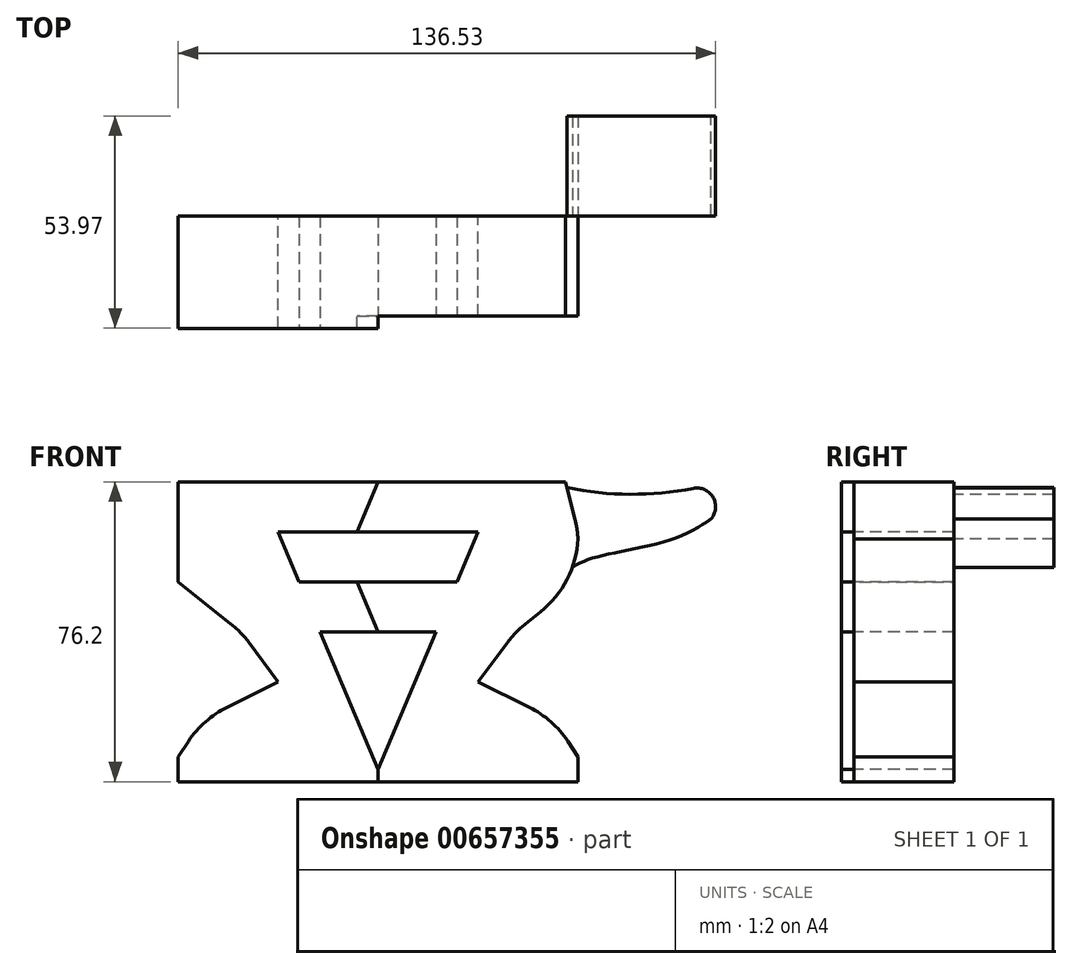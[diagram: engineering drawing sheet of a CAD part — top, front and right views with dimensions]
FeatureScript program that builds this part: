
annotation { "Feature Type Name" : "Feature", "Feature Type Description" : "" }
export const myFeature = defineFeature(function(context is Context, id is Id, definition is map)
    precondition{}
    {
        {
            var Q0;
            Q0=qCreatedBy(makeId("Front.planeOp"),FACE);
            var sketch = newSketch(context, id + "F0", { "sketchPlane" : qUnion([Q0])});
            skLineSegment(sketch, "E0.bottom", {"start": v(50.8, 38.1) * mm, "end": v(-50.8, 38.1) * mm, "construction": true});
            skLineSegment(sketch, "E0.top", {"start": v(50.8, -38.1) * mm, "end": v(-50.8, -38.1) * mm});
            skLineSegment(sketch, "E0.left", {"start": v(50.8, 38.1) * mm, "end": v(50.8, -38.1) * mm, "construction": true});
            skLineSegment(sketch, "E0.right", {"start": v(-50.8, 38.1) * mm, "end": v(-50.8, -38.1) * mm, "construction": true});
            skPoint(sketch, "E0.middle", {"position": v(0, 0) * mm});
            skLineSegment(sketch, "E1", {"start": v(0, 38.1) * mm, "end": v(0, -38.1) * mm, "construction": true});
            skLineSegment(sketch, "E2", {"start": v(-50.8, 0) * mm, "end": v(50.8, 0) * mm, "construction": true});
            skLineSegment(sketch, "E3", {"start": v(-50.8, 12.7) * mm, "end": v(50.8, 12.7) * mm, "construction": true});
            skLineSegment(sketch, "E4", {"start": v(-50.8, -12.7) * mm, "end": v(50.8, -12.7) * mm, "construction": true});
            skLineSegment(sketch, "E5", {"start": v(-25.4, 38.1) * mm, "end": v(-25.4, -38.1) * mm, "construction": true});
            skLineSegment(sketch, "E6", {"start": v(25.4, 38.1) * mm, "end": v(25.4, -38.1) * mm, "construction": true});
            skLineSegment(sketch, "E7", {"start": v(-50.8, 38.1) * mm, "end": v(-50.8, 12.7) * mm});
            skLineSegment(sketch, "E8", {"start": v(50.8, 38.1) * mm, "end": v(50.8, 12.7) * mm});
            skLineSegment(sketch, "E9", {"start": v(-50.8, 38.1) * mm, "end": v(50.8, 38.1) * mm});
            skLineSegment(sketch, "E10", {"start": v(-50.8, 12.7) * mm, "end": v(-25.4, -12.7) * mm, "construction": true});
            skLineSegment(sketch, "E11", {"start": v(50.8, 12.7) * mm, "end": v(25.4, -12.7) * mm, "construction": true});
            skLineSegment(sketch, "E12", {"start": v(-25.4, -12.7) * mm, "end": v(-50.8, -31.75) * mm, "construction": true});
            skLineSegment(sketch, "E13", {"start": v(-50.8, -31.75) * mm, "end": v(-50.8, -38.1) * mm});
            skLineSegment(sketch, "E14", {"start": v(25.4, -12.7) * mm, "end": v(50.8, -31.75) * mm, "construction": true});
            skLineSegment(sketch, "E15", {"start": v(50.8, -31.75) * mm, "end": v(50.8, -38.1) * mm});
            skLineSegment(sketch, "E16", {"start": v(-50.8, -38.1) * mm, "end": v(50.8, -38.1) * mm});
            skLineSegment(sketch, "E17", {"start": v(-50.8, 25.4) * mm, "end": v(50.8, 25.4) * mm, "construction": true});
            skLineSegment(sketch, "E18", {"start": v(-50.8, -31.75) * mm, "end": v(50.8, -31.75) * mm, "construction": true});
            skLineSegment(sketch, "E19", {"start": v(47.63, 38.1) * mm, "end": v(50.8, 25.4) * mm});
            skLineSegment(sketch, "E20", {"start": v(50.8, 12.7) * mm, "end": v(34.93, 0) * mm});
            skLineSegment(sketch, "E21", {"start": v(34.93, 0) * mm, "end": v(25.4, -12.7) * mm});
            skLineSegment(sketch, "E22", {"start": v(-50.8, 12.7) * mm, "end": v(-34.93, 0) * mm});
            skLineSegment(sketch, "E23", {"start": v(-34.93, 0) * mm, "end": v(-25.4, -12.7) * mm});
            skLineSegment(sketch, "E24", {"start": v(25.4, -12.7) * mm, "end": v(44.45, -22.22) * mm});
            skLineSegment(sketch, "E25", {"start": v(44.45, -22.22) * mm, "end": v(50.8, -31.75) * mm});
            skLineSegment(sketch, "E26", {"start": v(-25.4, -12.7) * mm, "end": v(-44.45, -22.22) * mm});
            skLineSegment(sketch, "E27", {"start": v(-44.45, -22.22) * mm, "end": v(-50.8, -31.75) * mm});
            skLineSegment(sketch, "E28", {"start": v(-50.8, -22.23) * mm, "end": v(50.8, -22.22) * mm, "construction": true});
            skSolve(sketch);
        }
        {
            var Q0;
            {var subQ2=sQuery(id+"F0.wireOp",EDGE,"E7");Q0=makeQuery(id+"F0.imprint","IMPRINT",FACE,{"disambiguationData":[TD([[makeQuery(id+"F0.imprint","IMPRINT",EDGE,{"derivedFrom":subQ2}),1.0]])]});}
            extrude(context, id + "F1", {"entities" : qUnion([Q0]), "depth" : 25.4 * mm, "offsetDistance" : 25.4 * mm});
        }
        {
            var Q0;
            Q0=makeQuery(id+"F1.opExtrude","SWEPT_EDGE",EDGE,{"disambiguationData":[OSD([sQuery(id+"F0.wireOp",EDGE,"E8"),sQuery(id+"F0.wireOp",EDGE,"E19")])]});
            var Q1;
            Q1=makeQuery(id+"F1.opExtrude","SWEPT_EDGE",EDGE,{"disambiguationData":[OSD([sQuery(id+"F0.wireOp",EDGE,"E8"),sQuery(id+"F0.wireOp",EDGE,"E20")])]});
            var Q2;
            Q2=makeQuery(id+"F1.opExtrude","SWEPT_EDGE",EDGE,{"disambiguationData":[OSD([sQuery(id+"F0.wireOp",EDGE,"E24"),sQuery(id+"F0.wireOp",EDGE,"E25")])]});
            var Q3;
            Q3=makeQuery(id+"F1.opExtrude","SWEPT_EDGE",EDGE,{"disambiguationData":[OSD([sQuery(id+"F0.wireOp",EDGE,"E20"),sQuery(id+"F0.wireOp",EDGE,"E21")])]});
            fillet(context, id + "F2", {"entities" : qUnion([Q0, Q1, Q2, Q3]), "radius" : 25.4 * mm, "tangentPropagation" : true, "allowEdgeOverflow" : false});
        }
        {
            var Q0;
            Q0=makeQuery(id+"F1.opExtrude","CAP_FACE",FACE,{"disambiguationData":[OSD([sQuery(id+"F0.wireOp",EDGE,"E7"),sQuery(id+"F0.wireOp",EDGE,"E8"),sQuery(id+"F0.wireOp",EDGE,"E9"),sQuery(id+"F0.wireOp",EDGE,"E13"),sQuery(id+"F0.wireOp",EDGE,"E15"),sQuery(id+"F0.wireOp",EDGE,"E16"),sQuery(id+"F0.wireOp",EDGE,"E19"),sQuery(id+"F0.wireOp",EDGE,"E20"),sQuery(id+"F0.wireOp",EDGE,"E21"),sQuery(id+"F0.wireOp",EDGE,"E22"),sQuery(id+"F0.wireOp",EDGE,"E23"),sQuery(id+"F0.wireOp",EDGE,"E24"),sQuery(id+"F0.wireOp",EDGE,"E25"),sQuery(id+"F0.wireOp",EDGE,"E26"),sQuery(id+"F0.wireOp",EDGE,"E27")])],"isStart":true});
            var sketch = newSketch(context, id + "F3", { "sketchPlane" : qUnion([Q0])});
            skLineSegment(sketch, "E29.bottom", {"start": v(-47.63, 38.1) * mm, "end": v(-85.72, 38.1) * mm, "construction": true});
            skLineSegment(sketch, "E29.top", {"start": v(-47.62, 12.7) * mm, "end": v(-85.72, 12.7) * mm, "construction": true});
            skLineSegment(sketch, "E29.left", {"start": v(-47.63, 38.1) * mm, "end": v(-47.63, 12.7) * mm, "construction": true});
            skLineSegment(sketch, "E29.right", {"start": v(-85.72, 38.1) * mm, "end": v(-85.72, 12.7) * mm, "construction": true});
            skLineSegment(sketch, "E30", {"start": v(-47.62, 34.92) * mm, "end": v(-85.72, 34.92) * mm, "construction": true});
            skArc(sketch, "E31", {"start": v(-80.05, 36.43) * mm, "mid": v(-85.61, 32.79) * mm, "end": v(-82.13, 27.13) * mm});
            skArc(sketch, "E32", {"start": v(-80.5, 36.51) * mm, "mid": v(-64.05, 34.93) * mm, "end": v(-47.63, 36.68) * mm});
            skLineSegment(sketch, "E33", {"start": v(-48.42, 34.92) * mm, "end": v(-48.42, 38.1) * mm, "construction": true});
            skPoint(sketch, "E34", {"position": v(-48.42, 36.51) * mm});
            skLineSegment(sketch, "E35", {"start": v(-48.42, 36.51) * mm, "end": v(-85.72, 36.51) * mm, "construction": true});
            skCircle(sketch, "E36", {"center": v(-113.4, -96.09) * mm, "radius": 127.13 * mm, "construction": true});
            skCircle(sketch, "E37", {"center": v(-80.96, 31.75) * mm, "radius": 4.76 * mm, "construction": true});
            skFitSpline(sketch, "E38", {"points": [v(-49.32, 16.36) * mm, v(-56.41, 19.23) * mm, v(-72.92, 22.96) * mm, v(-84.58, 28.66) * mm], "startDerivative": vector(-24.27, 15.2) * mm, "endDerivative": vector(-28.85, 20.7) * mm});
            skSolve(sketch);
        }
        {
            var Q0;
            {var subQ1=sQuery(id+"F3.wireOp",EDGE,"E31");var subQ10=sQuery(id+"F3.wireOp",EDGE,"E32");var subQ14=makeQuery(id+"F3.imprint","INTERSECT",VERTEX,{"derivedFrom":[subQ1,subQ10]});Q0=makeQuery(id+"F3.imprint","IMPRINT",FACE,{"disambiguationData":[TD([[makeQuery(id+"F3.imprint","IMPRINT",EDGE,{"disambiguationData":[TD([[subQ14,-1.0]])],"derivedFrom":subQ1}),1.0]])]});}
            extrude(context, id + "F4", {"entities" : qUnion([Q0]), "depth" : 25.4 * mm, "offsetDistance" : 25.4 * mm});
        }
        {
            var Q0;
            Q0=makeQuery(id+"F1.opExtrude","CAP_FACE",FACE,{"disambiguationData":[OSD([sQuery(id+"F0.wireOp",EDGE,"E7"),sQuery(id+"F0.wireOp",EDGE,"E8"),sQuery(id+"F0.wireOp",EDGE,"E9"),sQuery(id+"F0.wireOp",EDGE,"E13"),sQuery(id+"F0.wireOp",EDGE,"E15"),sQuery(id+"F0.wireOp",EDGE,"E16"),sQuery(id+"F0.wireOp",EDGE,"E19"),sQuery(id+"F0.wireOp",EDGE,"E20"),sQuery(id+"F0.wireOp",EDGE,"E21"),sQuery(id+"F0.wireOp",EDGE,"E22"),sQuery(id+"F0.wireOp",EDGE,"E23"),sQuery(id+"F0.wireOp",EDGE,"E24"),sQuery(id+"F0.wireOp",EDGE,"E25"),sQuery(id+"F0.wireOp",EDGE,"E26"),sQuery(id+"F0.wireOp",EDGE,"E27")])],"isStart":false});
            var sketch = newSketch(context, id + "F5", { "sketchPlane" : qUnion([Q0])});
            skLineSegment(sketch, "E39", {"start": v(0, 38.1) * mm, "end": v(0, -38.1) * mm, "construction": true});
            skLineSegment(sketch, "E40", {"start": v(-35.2, 0) * mm, "end": v(35.2, 0) * mm, "construction": true});
            skLineSegment(sketch, "E41", {"start": v(-50.8, 25.4) * mm, "end": v(50.04, 25.4) * mm, "construction": true});
            skLineSegment(sketch, "E42", {"start": v(-50.8, 12.7) * mm, "end": v(47.67, 12.7) * mm, "construction": true});
            skLineSegment(sketch, "E43", {"start": v(-25.4, 25.4) * mm, "end": v(25.4, 25.4) * mm});
            skLineSegment(sketch, "E44", {"start": v(20.05, 12.7) * mm, "end": v(-20.05, 12.7) * mm});
            skLineSegment(sketch, "E45", {"start": v(-14.7, 0) * mm, "end": v(14.7, 0) * mm});
            skLineSegment(sketch, "E46", {"start": v(25.4, 25.4) * mm, "end": v(0, -34.93) * mm, "construction": true});
            skLineSegment(sketch, "E47", {"start": v(0, -34.93) * mm, "end": v(-25.4, 25.4) * mm, "construction": true});
            skLineSegment(sketch, "E48", {"start": v(-10.07, -11) * mm, "end": v(10.07, -11) * mm, "construction": true});
            skPoint(sketch, "E49", {"position": v(0, -11) * mm});
            skLineSegment(sketch, "E50", {"start": v(-25.4, 25.4) * mm, "end": v(-20.05, 12.7) * mm});
            skLineSegment(sketch, "E51", {"start": v(25.4, 25.4) * mm, "end": v(20.05, 12.7) * mm});
            skLineSegment(sketch, "E52", {"start": v(-14.7, 0) * mm, "end": v(0, -34.93) * mm});
            skLineSegment(sketch, "E53", {"start": v(14.7, 0) * mm, "end": v(0, -34.93) * mm});
            skSolve(sketch);
        }
        {
            var Q0;
            Q0 = qSketchRegion(id + "F5", true);
            extrude(context, id + "F6", {"entities" : qUnion([Q0]), "operationType" : NewBodyOperationType.REMOVE, "endBound" : BoundingType.THROUGH_ALL, "oppositeDirection" : true, "depth" : 6.35 * mm, "offsetDistance" : 25.4 * mm});
        }
        {
            var Q0;
            Q0=makeQuery(id+"F1.opExtrude","CAP_FACE",FACE,{"disambiguationData":[OSD([sQuery(id+"F0.wireOp",EDGE,"E7"),sQuery(id+"F0.wireOp",EDGE,"E8"),sQuery(id+"F0.wireOp",EDGE,"E9"),sQuery(id+"F0.wireOp",EDGE,"E13"),sQuery(id+"F0.wireOp",EDGE,"E15"),sQuery(id+"F0.wireOp",EDGE,"E16"),sQuery(id+"F0.wireOp",EDGE,"E19"),sQuery(id+"F0.wireOp",EDGE,"E20"),sQuery(id+"F0.wireOp",EDGE,"E21"),sQuery(id+"F0.wireOp",EDGE,"E22"),sQuery(id+"F0.wireOp",EDGE,"E23"),sQuery(id+"F0.wireOp",EDGE,"E24"),sQuery(id+"F0.wireOp",EDGE,"E25"),sQuery(id+"F0.wireOp",EDGE,"E26"),sQuery(id+"F0.wireOp",EDGE,"E27")])],"isStart":false});
            var sketch = newSketch(context, id + "F7", { "sketchPlane" : qUnion([Q0])});
            skLineSegment(sketch, "E54", {"start": v(0, -38.1) * mm, "end": v(0, 38.1) * mm, "construction": true});
            skLineSegment(sketch, "E55", {"start": v(0, 0) * mm, "end": v(-5.35, 12.7) * mm});
            skLineSegment(sketch, "E56", {"start": v(0, 38.1) * mm, "end": v(-5.35, 25.4) * mm});
            skLineSegment(sketch, "E57", {"start": v(0, -38.1) * mm, "end": v(0, -34.93) * mm});
            skLineSegment(sketch, "E58", {"start": v(0, -34.93) * mm, "end": v(-14.7, 0) * mm});
            skLineSegment(sketch, "E59", {"start": v(-14.7, 0) * mm, "end": v(0, 0) * mm});
            skLineSegment(sketch, "E60", {"start": v(-5.35, 12.7) * mm, "end": v(-20.05, 12.7) * mm});
            skLineSegment(sketch, "E61", {"start": v(-20.05, 12.7) * mm, "end": v(-25.4, 25.4) * mm});
            skLineSegment(sketch, "E62", {"start": v(-25.4, 25.4) * mm, "end": v(-5.35, 25.4) * mm});
            skLineSegment(sketch, "E63", {"start": v(0, 38.1) * mm, "end": v(-50.8, 38.1) * mm});
            skLineSegment(sketch, "E64", {"start": v(-50.8, 38.1) * mm, "end": v(-50.8, 12.7) * mm});
            skLineSegment(sketch, "E65", {"start": v(-50.8, 12.7) * mm, "end": v(-34.93, 0) * mm});
            skLineSegment(sketch, "E66", {"start": v(-34.93, 0) * mm, "end": v(-25.4, -12.7) * mm});
            skLineSegment(sketch, "E67", {"start": v(-25.4, -12.7) * mm, "end": v(-44.45, -22.23) * mm});
            skLineSegment(sketch, "E68", {"start": v(-44.45, -22.23) * mm, "end": v(-50.8, -31.75) * mm});
            skLineSegment(sketch, "E69", {"start": v(-50.8, -31.75) * mm, "end": v(-50.8, -38.1) * mm});
            skLineSegment(sketch, "E70", {"start": v(-50.8, -38.1) * mm, "end": v(0, -38.1) * mm});
            skSolve(sketch);
        }
        {
            var Q0;
            Q0=makeQuery(id+"F7.imprint","IMPRINT",FACE,{"disambiguationData":[TD([[makeQuery(id+"F7.imprint","IMPRINT",EDGE,{"derivedFrom":sQuery(id+"F7.wireOp",EDGE,"E55")}),1.0]])]});
            extrude(context, id + "F8", {"entities" : qUnion([Q0]), "operationType" : NewBodyOperationType.ADD, "depth" : 3.17 * mm, "offsetDistance" : 25.4 * mm});
        }
        {
            var Q0;
            Q0=makeQuery(id+"F8.boolean.opBoolean","MERGE",EDGE,{"derivedFrom":[makeQuery(id+"F1.opExtrude","SWEPT_EDGE",EDGE,{"disambiguationData":[OSD([sQuery(id+"F0.wireOp",EDGE,"E22"),sQuery(id+"F0.wireOp",EDGE,"E23")])]}),makeQuery(id+"F8.opExtrude","SWEPT_EDGE",EDGE,{"disambiguationData":[OSD([sQuery(id+"F7.wireOp",EDGE,"E65"),sQuery(id+"F7.wireOp",EDGE,"E66")])]})]});
            var Q1;
            Q1=makeQuery(id+"F8.boolean.opBoolean","MERGE",EDGE,{"derivedFrom":[makeQuery(id+"F1.opExtrude","SWEPT_EDGE",EDGE,{"disambiguationData":[OSD([sQuery(id+"F0.wireOp",EDGE,"E26"),sQuery(id+"F0.wireOp",EDGE,"E27")])]}),makeQuery(id+"F8.opExtrude","SWEPT_EDGE",EDGE,{"disambiguationData":[OSD([sQuery(id+"F7.wireOp",EDGE,"E67"),sQuery(id+"F7.wireOp",EDGE,"E68")])]})]});
            fillet(context, id + "F9", {"entities" : qUnion([Q0, Q1]), "radius" : 25.4 * mm, "tangentPropagation" : true, "allowEdgeOverflow" : false});
        }
    });
